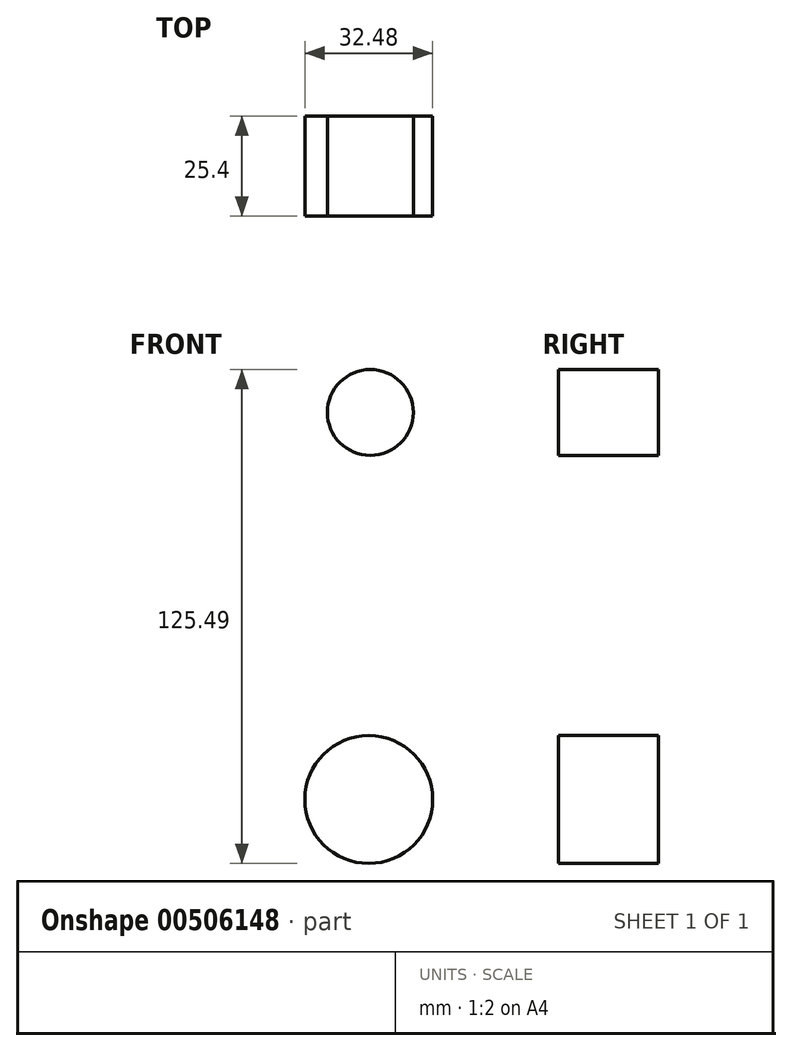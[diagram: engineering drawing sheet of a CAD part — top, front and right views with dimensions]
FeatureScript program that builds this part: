
annotation { "Feature Type Name" : "Feature", "Feature Type Description" : "" }
export const myFeature = defineFeature(function(context is Context, id is Id, definition is map)
    precondition{}
    {
        {
            var Q0;
            Q0=qCreatedBy(makeId("Front.planeOp"),FACE);
            var sketch = newSketch(context, id + "F0", { "sketchPlane" : qUnion([Q0])});
            skLineSegment(sketch, "E0", {"start": v(0, 57.65) * mm, "end": v(0, -19.78) * mm});
            skLineSegment(sketch, "E1", {"start": v(16.5, 57.07) * mm, "end": v(16.5, -19.78) * mm});
            skCircle(sketch, "E2", {"center": v(8.11, -33.85) * mm, "radius": 16.24 * mm});
            skCircle(sketch, "E3", {"center": v(8.5, 64.49) * mm, "radius": 10.9 * mm});
            skSolve(sketch);
        }
        {
            var Q0;
            Q0 = qSketchRegion(id + "F0", true);
            extrude(context, id + "F1", {"entities" : qUnion([Q0]), "depth" : 25.4 * mm, "offsetDistance" : 25.4 * mm});
        }
    });
